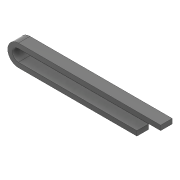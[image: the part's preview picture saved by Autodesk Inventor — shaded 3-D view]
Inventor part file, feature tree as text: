
AUTODESK INVENTOR PART (.ipt)
format: ipt  version: 2020 (Build 240168000, 168)  size: 96,768 bytes
history: native  units: mm
features: extrude x1, sketch x1
ambient origin geometry x8: Origin, YZ Plane, XZ Plane, XY Plane, X Axis, Y Axis, Z Axis, Center Point
bodies: Solid1 (feature_tree)
feature tree (2):
  extrude  "Extrusion1"  Depth=20.0mm
  sketch  "Sketch1"  dims[d0=90.0mm d1=20.0mm d2=20.0mm d4=500.0mm d5=49.0mm d6=0.0mm d9=600.0mm]
